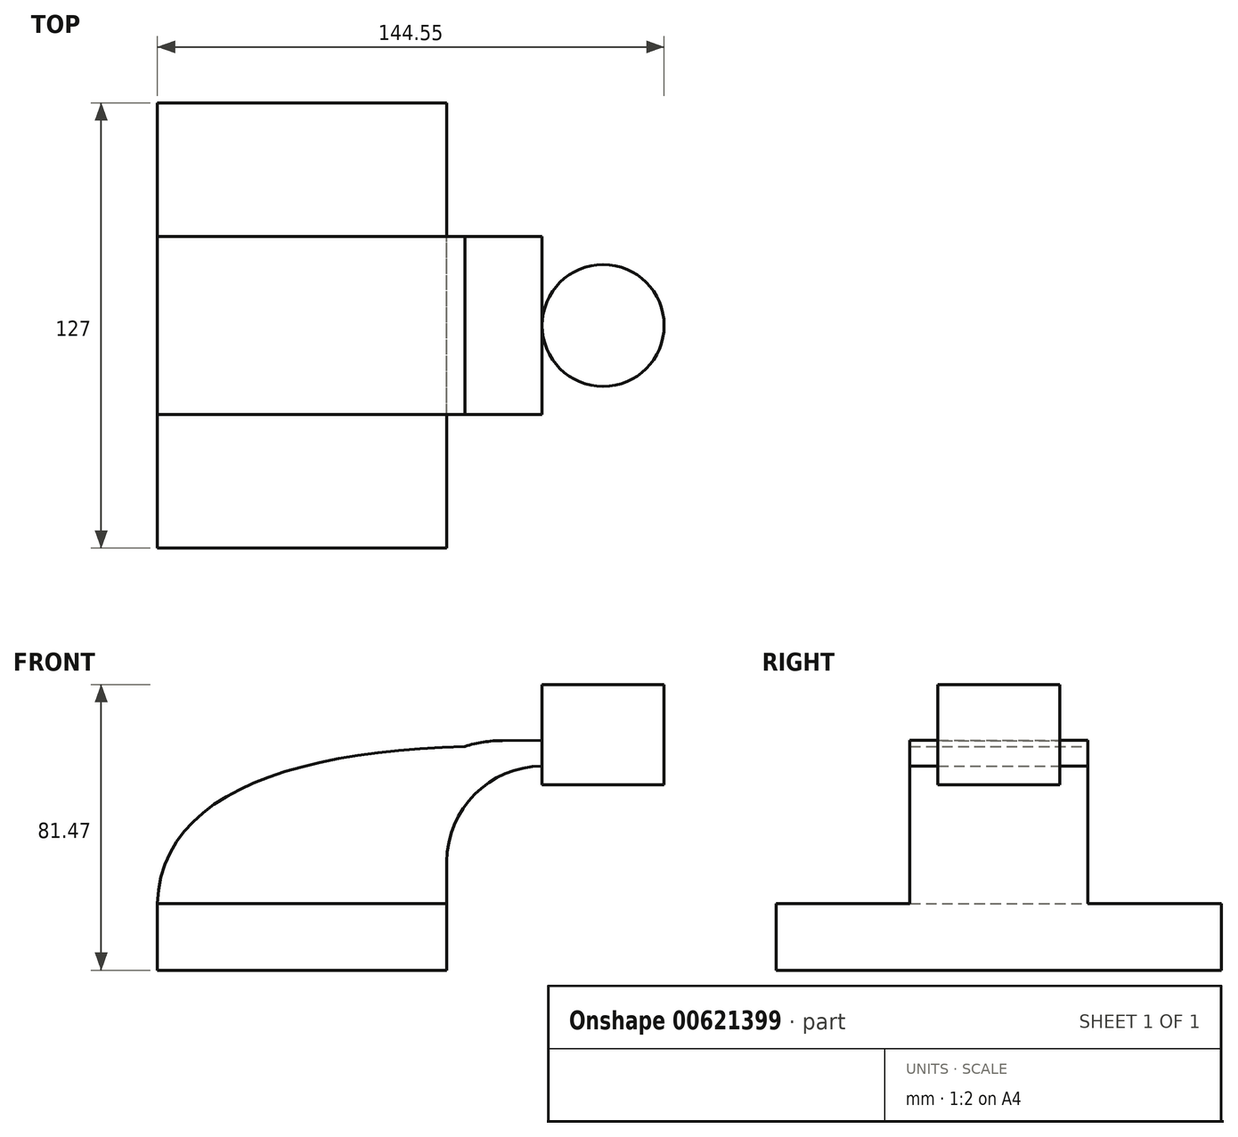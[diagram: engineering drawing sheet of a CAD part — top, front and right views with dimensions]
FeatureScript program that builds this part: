
annotation { "Feature Type Name" : "Feature", "Feature Type Description" : "" }
export const myFeature = defineFeature(function(context is Context, id is Id, definition is map)
    precondition{}
    {
        {
            var Q0;
            Q0=qCreatedBy(makeId("Front.planeOp"),FACE);
            var sketch = newSketch(context, id + "F0", { "sketchPlane" : qUnion([Q0])});
            skLineSegment(sketch, "E0.bottom", {"start": v(-41.28, -9.52) * mm, "end": v(41.28, -9.52) * mm});
            skLineSegment(sketch, "E0.top", {"start": v(-41.28, 9.52) * mm, "end": v(41.28, 9.52) * mm});
            skLineSegment(sketch, "E0.left", {"start": v(-41.28, -9.52) * mm, "end": v(-41.28, 9.53) * mm});
            skLineSegment(sketch, "E0.right", {"start": v(41.28, -9.52) * mm, "end": v(41.28, 9.52) * mm});
            skPoint(sketch, "E0.middle", {"position": v(0, 0) * mm});
            skPoint(sketch, "E1.middle", {"position": v(85.72, 57.65) * mm});
            skLineSegment(sketch, "E2", {"start": v(41.28, 9.52) * mm, "end": v(41.28, 21.4) * mm});
            skLineSegment(sketch, "E3.0", {"start": v(57.15, 56) * mm, "end": v(85.82, 56.28) * mm});
            skArc(sketch, "E3.1", {"start": v(22.23, 21.07) * mm, "mid": v(32.45, 45.77) * mm, "end": v(57.15, 56) * mm});
            skLineSegment(sketch, "E3.2", {"start": v(22.23, 11.87) * mm, "end": v(22.23, 21.07) * mm});
            skLineSegment(sketch, "E4", {"start": v(85.91, 54.9) * mm, "end": v(85.72, 57.65) * mm});
            skFitSpline(sketch, "E5", {"points": [v(-41.28, 9.53) * mm, v(46.46, 54.32) * mm], "startDerivative": vector(2.75, 92.23) * mm, "endDerivative": vector(150.49, 3.98) * mm});
            skArc(sketch, "E6", {"start": v(41.28, 21.4) * mm, "mid": v(50.33, 41.7) * mm, "end": v(71.48, 48.5) * mm});
            skPoint(sketch, "E6.endSnap0", {"position": v(71.48, 56.14) * mm});
            skLineSegment(sketch, "E7", {"start": v(71.48, 48.5) * mm, "end": v(85.83, 48.5) * mm});
            skLineSegment(sketch, "E8.bottom", {"start": v(103.27, 43.36) * mm, "end": v(68.48, 43.36) * mm});
            skLineSegment(sketch, "E8.top", {"start": v(103.27, 71.94) * mm, "end": v(68.48, 71.94) * mm});
            skLineSegment(sketch, "E8.left", {"start": v(103.27, 43.36) * mm, "end": v(103.27, 71.94) * mm});
            skLineSegment(sketch, "E8.right", {"start": v(68.48, 43.36) * mm, "end": v(68.48, 71.94) * mm});
            skPoint(sketch, "E8.middle", {"position": v(85.87, 57.65) * mm});
            skLineSegment(sketch, "E9", {"start": v(85.87, 43.36) * mm, "end": v(85.87, 71.94) * mm});
            skSolve(sketch);
        }
        {
            var Q0;
            Q0=makeQuery(id+"F0.imprint","IMPRINT",FACE,{"disambiguationData":[TD([[makeQuery(id+"F0.imprint","IMPRINT",EDGE,{"derivedFrom":sQuery(id+"F0.wireOp",EDGE,"E0.bottom")}),1.0]])]});
            extrude(context, id + "F1", {"entities" : qUnion([Q0]), "endBound" : BoundingType.SYMMETRIC, "depth" : 127 * mm, "offsetDistance" : 25.4 * mm});
        }
        {
            var Q0;
            {var subQ1=sQuery(id+"F0.wireOp",EDGE,"E2");Q0=makeQuery(id+"F0.imprint","IMPRINT",FACE,{"disambiguationData":[TD([[makeQuery(id+"F0.imprint","IMPRINT",EDGE,{"derivedFrom":subQ1}),1.0]])]});}
            var Q1;
            {var subQ8=sQuery(id+"F0.wireOp",EDGE,"E1.bottom");Q1=makeQuery(id+"F0.imprint","IMPRINT",FACE,{"disambiguationData":[TD([[makeQuery(id+"F0.imprint","IMPRINT",EDGE,{"derivedFrom":subQ8}),1.0]])]});}
            extrude(context, id + "F2", {"entities" : qUnion([Q0, Q1]), "operationType" : NewBodyOperationType.ADD, "endBound" : BoundingType.SYMMETRIC, "depth" : 50.8 * mm, "offsetDistance" : 25.4 * mm});
        }
        {
            var Q0;
            {var subQ4=sQuery(id+"F0.wireOp",EDGE,"E8.left");Q0=makeQuery(id+"F0.imprint","IMPRINT",FACE,{"disambiguationData":[TD([[makeQuery(id+"F0.imprint","IMPRINT",EDGE,{"derivedFrom":subQ4}),1.0]])]});}
            var Q1;
            Q1=sQuery(id+"F0.wireOp",EDGE,"E9");
            revolve(context, id + "F3", {"operationType" : NewBodyOperationType.ADD, "entities" : qUnion([Q0]), "axis" : qUnion([Q1]), "revolveType" : RevolveType.FULL});
        }
    });
